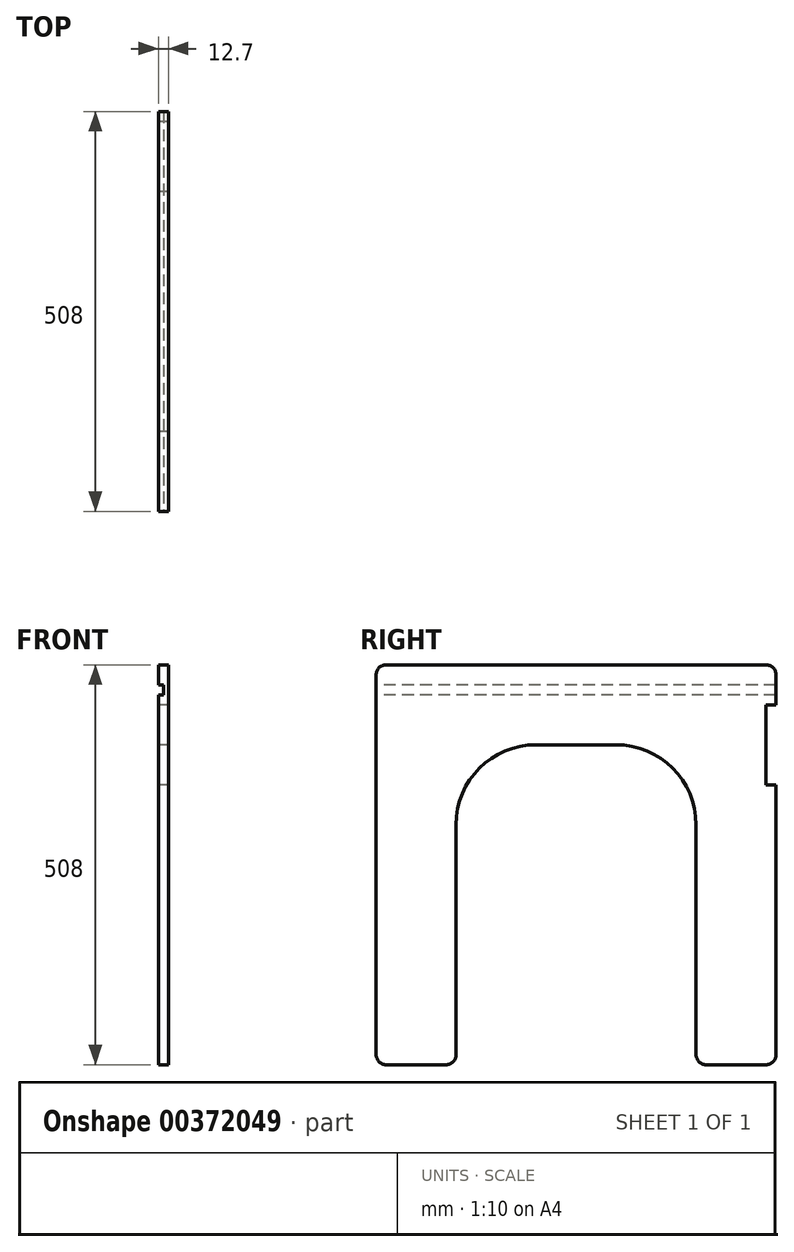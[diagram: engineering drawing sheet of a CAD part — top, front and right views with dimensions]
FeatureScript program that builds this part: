
annotation { "Feature Type Name" : "Feature", "Feature Type Description" : "" }
export const myFeature = defineFeature(function(context is Context, id is Id, definition is map)
    precondition{}
    {
        {
            var Q0;
            Q0=qCreatedBy(makeId("Right.planeOp"),FACE);
            var sketch = newSketch(context, id + "F0", { "sketchPlane" : qUnion([Q0])});
            skLineSegment(sketch, "E0.bottom", {"start": v(-88.9, 0) * mm, "end": v(-12.7, 0) * mm});
            skLineSegment(sketch, "E0.top", {"start": v(-88.9, 508) * mm, "end": v(393.7, 508) * mm});
            skLineSegment(sketch, "E0.left", {"start": v(-101.6, 12.7) * mm, "end": v(-101.6, 495.3) * mm});
            skLineSegment(sketch, "E0.right", {"start": v(406.4, 12.7) * mm, "end": v(406.4, 355.6) * mm});
            skLineSegment(sketch, "E1.top", {"start": v(203.2, 406.4) * mm, "end": v(101.6, 406.4) * mm});
            skLineSegment(sketch, "E1.left", {"start": v(304.8, 12.7) * mm, "end": v(304.8, 304.8) * mm});
            skLineSegment(sketch, "E1.right", {"start": v(0, 12.7) * mm, "end": v(0, 304.8) * mm});
            skPoint(sketch, "E2.visualSharp", {"position": v(0, 406.4) * mm});
            skArc(sketch, "E2.filletArc", {"start": v(101.6, 406.4) * mm, "mid": v(29.76, 376.64) * mm, "end": v(0, 304.8) * mm});
            skPoint(sketch, "E3.visualSharp", {"position": v(304.8, 406.4) * mm});
            skArc(sketch, "E3.filletArc", {"start": v(304.8, 304.8) * mm, "mid": v(275.04, 376.64) * mm, "end": v(203.2, 406.4) * mm});
            skPoint(sketch, "E4.visualSharp", {"position": v(-101.6, 0) * mm});
            skArc(sketch, "E4.filletArc", {"start": v(-101.6, 12.7) * mm, "mid": v(-97.88, 3.72) * mm, "end": v(-88.9, 0) * mm});
            skLineSegment(sketch, "E5.trimOffspring", {"start": v(317.5, 0) * mm, "end": v(393.7, 0) * mm});
            skPoint(sketch, "E6.visualSharp", {"position": v(0, 0) * mm});
            skArc(sketch, "E6.filletArc", {"start": v(-12.7, 0) * mm, "mid": v(-3.72, 3.72) * mm, "end": v(0, 12.7) * mm});
            skPoint(sketch, "E7.visualSharp", {"position": v(304.8, 0) * mm});
            skArc(sketch, "E7.filletArc", {"start": v(304.8, 12.7) * mm, "mid": v(308.52, 3.72) * mm, "end": v(317.5, 0) * mm});
            skPoint(sketch, "E8.visualSharp", {"position": v(406.4, 0) * mm});
            skArc(sketch, "E8.filletArc", {"start": v(393.7, 0) * mm, "mid": v(402.68, 3.72) * mm, "end": v(406.4, 12.7) * mm});
            skPoint(sketch, "E9.visualSharp", {"position": v(406.4, 508) * mm});
            skArc(sketch, "E9.filletArc", {"start": v(406.4, 495.3) * mm, "mid": v(402.68, 504.28) * mm, "end": v(393.7, 508) * mm});
            skPoint(sketch, "E10.visualSharp", {"position": v(-101.6, 508) * mm});
            skArc(sketch, "E10.filletArc", {"start": v(-88.9, 508) * mm, "mid": v(-97.88, 504.28) * mm, "end": v(-101.6, 495.3) * mm});
            skLineSegment(sketch, "E11.bottom", {"start": v(406.4, 457.2) * mm, "end": v(393.7, 457.2) * mm});
            skLineSegment(sketch, "E11.top", {"start": v(406.4, 355.6) * mm, "end": v(393.7, 355.6) * mm});
            skLineSegment(sketch, "E11.right", {"start": v(393.7, 457.2) * mm, "end": v(393.7, 355.6) * mm});
            skLineSegment(sketch, "E12.trimOffspring", {"start": v(406.4, 457.2) * mm, "end": v(406.4, 495.3) * mm});
            skSolve(sketch);
        }
        {
            var Q0;
            Q0 = qSketchRegion(id + "F0", true);
            extrude(context, id + "F1", {"entities" : qUnion([Q0]), "depth" : 12.7 * mm});
        }
        {
            var Q0;
            Q0=makeQuery(id+"F1.opExtrude","CAP_FACE",FACE,{"disambiguationData":[OSD([sQuery(id+"F0.wireOp",EDGE,"E0.bottom"),sQuery(id+"F0.wireOp",EDGE,"E0.top"),sQuery(id+"F0.wireOp",EDGE,"E0.left"),sQuery(id+"F0.wireOp",EDGE,"E0.right"),sQuery(id+"F0.wireOp",EDGE,"E1.top"),sQuery(id+"F0.wireOp",EDGE,"E1.left"),sQuery(id+"F0.wireOp",EDGE,"E1.right"),sQuery(id+"F0.wireOp",EDGE,"E2.filletArc"),sQuery(id+"F0.wireOp",EDGE,"E3.filletArc"),sQuery(id+"F0.wireOp",EDGE,"E4.filletArc"),sQuery(id+"F0.wireOp",EDGE,"E5.trimOffspring"),sQuery(id+"F0.wireOp",EDGE,"E6.filletArc"),sQuery(id+"F0.wireOp",EDGE,"E7.filletArc"),sQuery(id+"F0.wireOp",EDGE,"E8.filletArc"),sQuery(id+"F0.wireOp",EDGE,"E9.filletArc"),sQuery(id+"F0.wireOp",EDGE,"E10.filletArc"),sQuery(id+"F0.wireOp",EDGE,"E11.bottom"),sQuery(id+"F0.wireOp",EDGE,"E11.top"),sQuery(id+"F0.wireOp",EDGE,"E11.right"),sQuery(id+"F0.wireOp",EDGE,"E12.trimOffspring")])],"isStart":true});
            var sketch = newSketch(context, id + "F2", { "sketchPlane" : qUnion([Q0])});
            skLineSegment(sketch, "E13.bottom", {"start": v(-406.4, 482.6) * mm, "end": v(101.6, 482.6) * mm});
            skLineSegment(sketch, "E13.top", {"start": v(-406.4, 469.9) * mm, "end": v(101.6, 469.9) * mm});
            skLineSegment(sketch, "E13.left", {"start": v(-406.4, 482.6) * mm, "end": v(-406.4, 469.9) * mm});
            skLineSegment(sketch, "E13.right", {"start": v(101.6, 482.6) * mm, "end": v(101.6, 469.9) * mm});
            skSolve(sketch);
        }
        {
            var Q0;
            Q0 = qSketchRegion(id + "F2", true);
            extrude(context, id + "F3", {"entities" : qUnion([Q0]), "operationType" : NewBodyOperationType.REMOVE, "oppositeDirection" : true, "depth" : 6.35 * mm});
        }
    });
